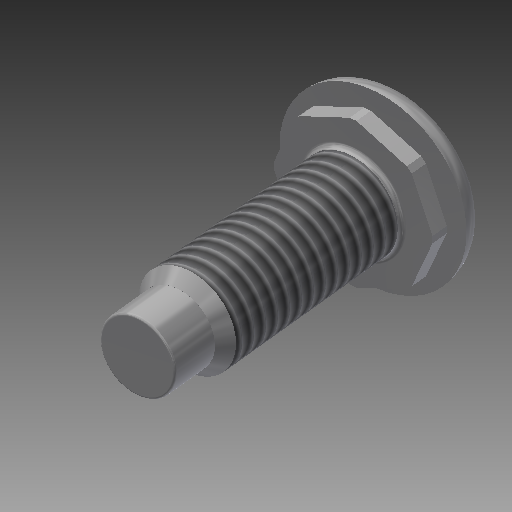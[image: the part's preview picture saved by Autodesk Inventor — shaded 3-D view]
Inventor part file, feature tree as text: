
AUTODESK INVENTOR PART (.ipt)
format: ipt  version: 2019 (Build 230136000, 136)  size: 297,472 bytes
history: native  units: in
note: dims shown in document units (in); Inventor stores cm internally (conversion verified against a paired STEP export)
features: chamfer x9, extrude x6, sketch x6, plane x3, fillet x2, thread x1
ambient origin geometry x8: Origin, YZ Plane, XZ Plane, XY Plane, X Axis, Y Axis, Z Axis, Center Point
bodies: Solid1 (feature_tree)
feature tree (27):
  plane  "Work Plane1"
  extrude  "Extrusion1"  Depth=20.0938in
  extrude  "Extrusion2"  Depth=0.1969in TaperAngle=0.0deg
  extrude  "Extrusion3"  Depth=0.8693in TaperAngle=0.0deg
  extrude  "Extrusion4"  Depth=0.0945in
  extrude  "Extrusion5"  Depth=0.0709in
  fillet  "Fillet1"  Radius=20.0938in
  extrude  "Extrusion6"  Depth=0.0276in TaperAngle=0.0deg
  fillet  "Fillet2"  Radius=0.748in
  chamfer  "Chamfer2"  Distance=0.1181in
  chamfer  "Chamfer3"  Distance=0.1181in
  chamfer  "Chamfer4"  Distance=0.0394in
  chamfer  "Chamfer5"  Distance=0.0197in
  chamfer  "Chamfer6"  Distance=0.0098in
  chamfer  "Chamfer7"  Distance=0.3937in
  chamfer  "Chamfer8"  Distance=0.0787in
  chamfer  "Chamfer9"  Distance=0.0197in
  plane  "Work Plane3"
  chamfer  "Chamfer10"  Distance=0.0787in Angle=45.0deg
  thread  "Thread1"  [1 undecoded]
  sketch  "Sketch1"  dims[d0=0.3031in d1=20.0938in]
  sketch  "Sketch2"  dims[d2=104.6482in d3=0.1969in d4=0.0in]
  sketch  "Sketch3"  dims[d5=0.3894in d6=0.8693in d7=0.0in]
  sketch  "Sketch4"  dims[d8=0.2283in d9=0.0945in]
  sketch  "Sketch5"  dims[d10=0.0709in d11=0.0in d12=0.4977in d14=20.0938in]
  sketch  "Sketch6"  dims[d15=104.6482in d16=0.0276in d17=0.0in d18=0.748in d19=0.1181in d20=0.0in d21=0.1181in d22=0.0394in d23=0.0197in d24=0.0098in d25=0.3937in d26=0.0787in d27=0.0in d28=0.0197in d32=0.0148in d33=0.0787in d34=45.0deg d35=0.0148in d36=0.0787in d37=45.0deg d38=0.0148in d39=0.0787in d40=45.0deg d41=0.0148in d42=0.0787in d43=45.0deg d44=0.0148in d45=0.0787in d46=45.0deg d47=0.0148in d48=0.0787in d49=45.0deg d50=0.0148in d51=0.0787in d52=45.0deg d53=0.0148in d54=0.0787in d55=45.0deg d56=90.0deg d57=-0.2982in d58=0.0431in d59=0.0511in d60=45.0deg d61=0.3937in d62=0.0in]
  plane  "Work Plane2"
note: 1 required parameter value undecoded (feature->parameter linkage not recoverable at this tier; creation-order binding heuristic only, values carry confidence <= 0.55)
